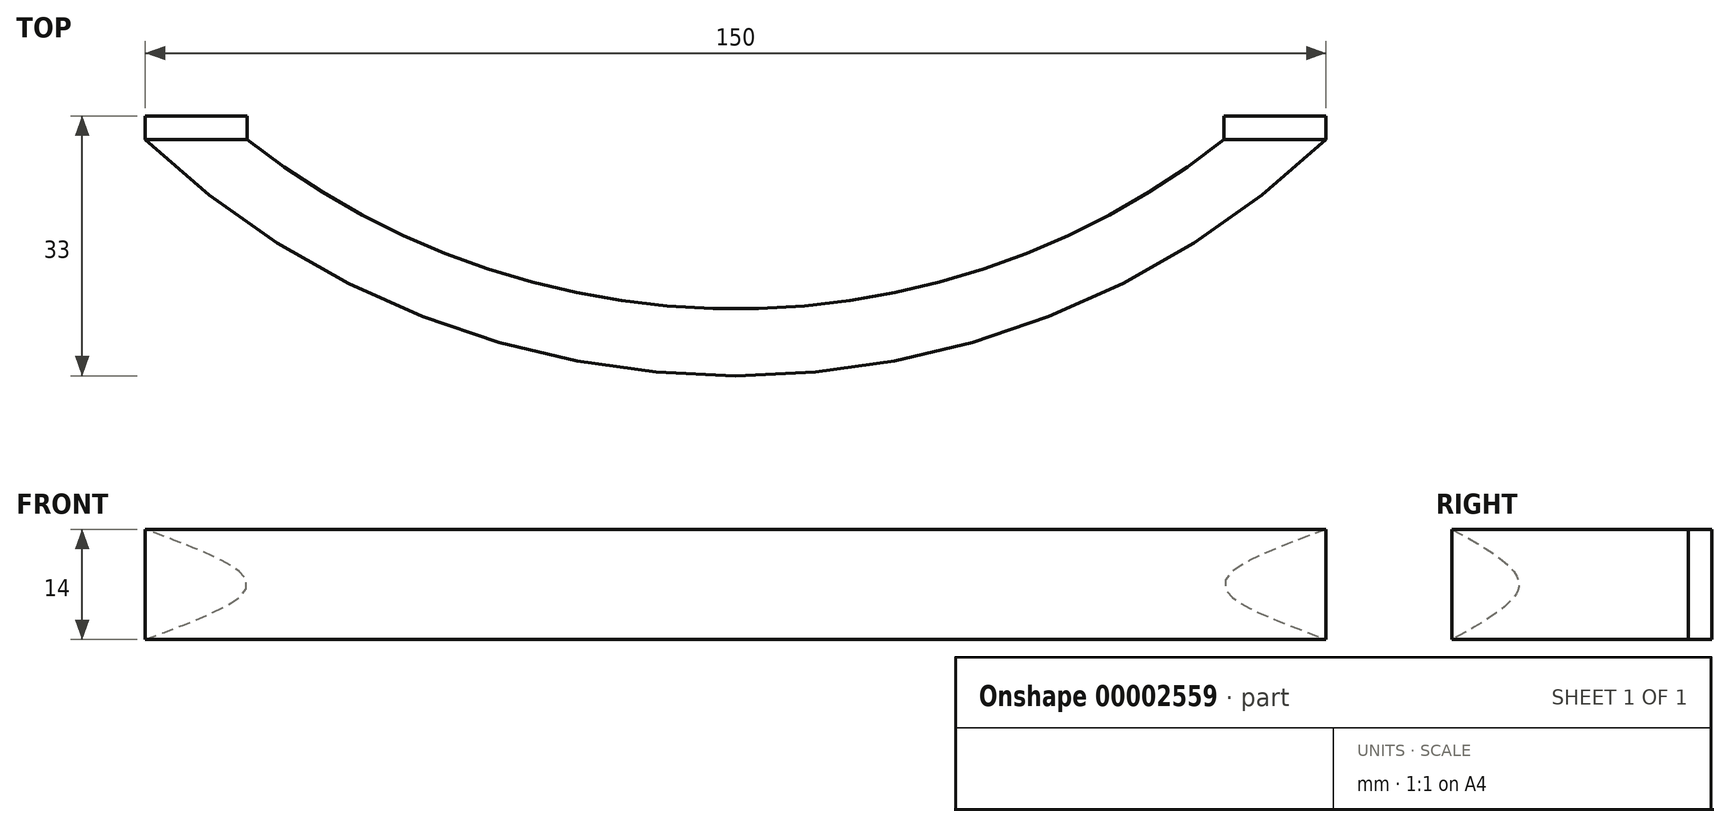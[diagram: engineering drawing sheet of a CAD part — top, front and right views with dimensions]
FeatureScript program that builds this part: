
annotation { "Feature Type Name" : "Feature", "Feature Type Description" : "" }
export const myFeature = defineFeature(function(context is Context, id is Id, definition is map)
    precondition{}
    {
        {
            var Q0;
            Q0=qCreatedBy(makeId("Top.planeOp"),FACE);
            var sketch = newSketch(context, id + "F0", { "sketchPlane" : qUnion([Q0])});
            skLineSegment(sketch, "E0", {"start": v(-75, 0) * mm, "end": v(75, 0) * mm, "construction": true});
            skLineSegment(sketch, "E1", {"start": v(0, 0) * mm, "end": v(0, -30) * mm, "construction": true});
            skArc(sketch, "E2", {"start": v(-75, 0) * mm, "mid": v(0, -30) * mm, "end": v(75, 0) * mm});
            skLineSegment(sketch, "E3", {"start": v(-75, 0) * mm, "end": v(-96, 20) * mm});
            skLineSegment(sketch, "E4", {"start": v(75, 0) * mm, "end": v(96, 20) * mm});
            skLineSegment(sketch, "E5", {"start": v(0, 0) * mm, "end": v(0, 20) * mm, "construction": true});
            skLineSegment(sketch, "E6", {"start": v(-96, 20) * mm, "end": v(96, 20) * mm, "construction": true});
            skLineSegment(sketch, "E7", {"start": v(96, 20) * mm, "end": v(90.14, 26.16) * mm, "construction": true});
            skSolve(sketch);
        }
        {
            var Q0;
            Q0=sQuery(id+"F0.wireOp",EDGE,"E7");
            cPlane(context, id + "F1", {"entities" : qUnion([Q0]), "cplaneType" : CPlaneType.LINE_ANGLE, "offset" : 150 * mm, "angle" : 90 * degree, "width" : 150 * mm, "height" : 150 * mm});
        }
        {
            var Q0;
            Q0=qCreatedBy(id+"F1.planeOp",FACE);
            var sketch = newSketch(context, id + "F2", { "sketchPlane" : qUnion([Q0])});
            skLineSegment(sketch, "E8.0", {"start": v(-51.72, 0) * mm, "end": v(-43.22, 0) * mm, "construction": true});
            skLineSegment(sketch, "E9", {"start": v(-51.72, -7) * mm, "end": v(-51.72, 7) * mm});
            skFitSpline(sketch, "E10", {"points": [v(-51.72, -7) * mm, v(-43.22, 0) * mm, v(-51.72, 7) * mm], "startDerivative": vector(25.5, 14) * mm, "endDerivative": vector(-25.5, 14) * mm});
            skSolve(sketch);
        }
        {
            var Q0;
            Q0=makeQuery(id+"F2.imprint","IMPRINT",FACE,{"disambiguationData":[TD([[makeQuery(id+"F2.imprint","IMPRINT",EDGE,{"derivedFrom":sQuery(id+"F2.wireOp",EDGE,"E9")}),-1.0]])]});
            var Q1;
            Q1=sQuery(id+"F0.wireOp",EDGE,"E4");
            var Q2;
            Q2=sQuery(id+"F0.wireOp",EDGE,"E2");
            var Q3;
            Q3=sQuery(id+"F0.wireOp",EDGE,"E3");
            sweep(context, id + "F3", {"profiles" : qUnion([Q0]), "path" : qUnion([Q1, Q2, Q3])});
        }
        {
            var Q0;
            Q0=qCreatedBy(makeId("Top.planeOp"),FACE);
            var sketch = newSketch(context, id + "F4", { "sketchPlane" : qUnion([Q0])});
            skLineSegment(sketch, "E11.bottom", {"start": v(-106.48, 0) * mm, "end": v(105.09, 0) * mm});
            skLineSegment(sketch, "E11.top", {"start": v(-106.48, 40.8) * mm, "end": v(105.09, 40.8) * mm});
            skLineSegment(sketch, "E11.left", {"start": v(-106.48, 0) * mm, "end": v(-106.48, 40.8) * mm});
            skLineSegment(sketch, "E11.right", {"start": v(105.09, 0) * mm, "end": v(105.09, 40.8) * mm});
            skSolve(sketch);
        }
        {
            var Q0;
            Q0=makeQuery(id+"F4.imprint","IMPRINT",FACE,{"disambiguationData":[TD([[makeQuery(id+"F4.imprint","IMPRINT",EDGE,{"derivedFrom":sQuery(id+"F4.wireOp",EDGE,"E11.bottom")}),1.0]])]});
            extrude(context, id + "F5", {"entities" : qUnion([Q0]), "operationType" : NewBodyOperationType.REMOVE, "endBound" : BoundingType.SYMMETRIC, "depth" : 50 * mm});
        }
        {
            var Q0;
            Q0=makeQuery(id+"F5.boolean.opBoolean","COPY",FACE,{"disambiguationData":[OD(0.0)],"derivedFrom":makeQuery(id+"F5.opExtrude","SWEPT_FACE",FACE,{"disambiguationData":[OSD([sQuery(id+"F4.wireOp",EDGE,"E11.bottom")])]})});
            var Q1;
            Q1=makeQuery(id+"F5.boolean.opBoolean","COPY",FACE,{"disambiguationData":[OD(1.0)],"derivedFrom":makeQuery(id+"F5.opExtrude","SWEPT_FACE",FACE,{"disambiguationData":[OSD([sQuery(id+"F4.wireOp",EDGE,"E11.bottom")])]})});
            extrude(context, id + "F6", {"entities" : qUnion([Q0, Q1]), "operationType" : NewBodyOperationType.ADD, "depth" : 3 * mm});
        }
    });
